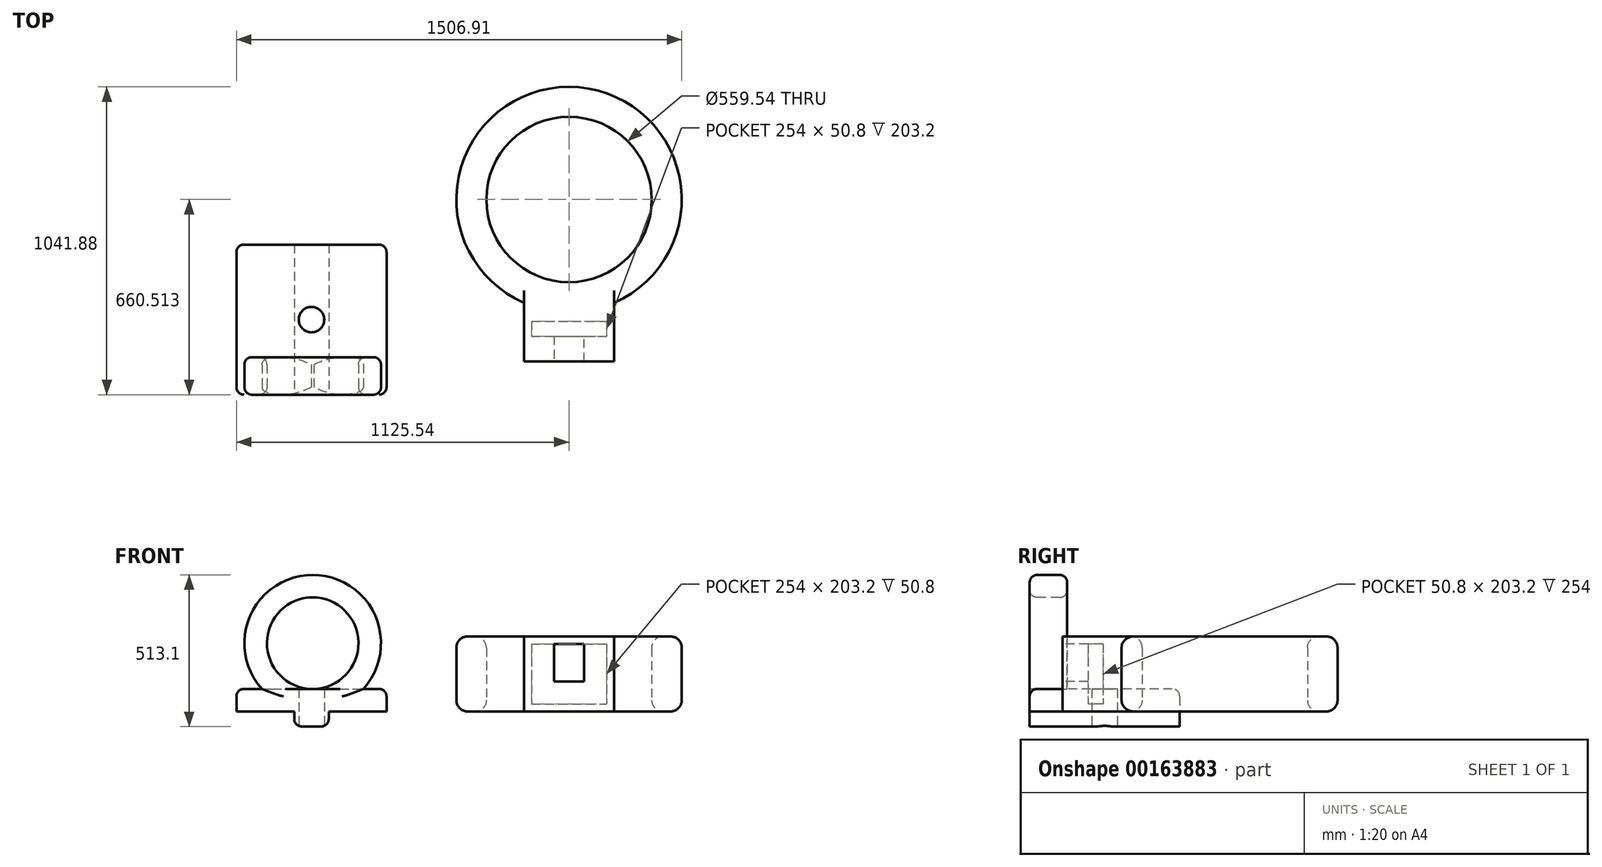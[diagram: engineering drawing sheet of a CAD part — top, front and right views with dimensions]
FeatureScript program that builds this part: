
annotation { "Feature Type Name" : "Feature", "Feature Type Description" : "" }
export const myFeature = defineFeature(function(context is Context, id is Id, definition is map)
    precondition{}
    {
        {
            var Q0;
            Q0=qCreatedBy(makeId("Top.planeOp"),FACE);
            var sketch = newSketch(context, id + "F0", { "sketchPlane" : qUnion([Q0])});
            skLineSegment(sketch, "E0.bottom", {"start": v(-152.4, 196.86) * mm, "end": v(152.4, 196.86) * mm});
            skLineSegment(sketch, "E0.top", {"start": v(-152.4, -6.34) * mm, "end": v(152.4, -6.34) * mm});
            skLineSegment(sketch, "E0.left", {"start": v(-152.4, 196.86) * mm, "end": v(-152.4, -6.34) * mm});
            skLineSegment(sketch, "E0.right", {"start": v(152.4, 196.86) * mm, "end": v(152.4, -6.34) * mm});
            skCircle(sketch, "E1", {"center": v(0, 542.32) * mm, "radius": 381.37 * mm});
            skCircle(sketch, "E2", {"center": v(0, 542.32) * mm, "radius": 279.77 * mm});
            skSolve(sketch);
        }
        {
            var Q0;
            {var subQ5=sQuery(id+"F0.wireOp",EDGE,"E0.bottom");Q0=makeQuery(id+"F0.imprint","IMPRINT",FACE,{"disambiguationData":[TD([[makeQuery(id+"F0.imprint","IMPRINT",EDGE,{"derivedFrom":subQ5}),1.0]])]});}
            var Q1;
            {var subQ0=sQuery(id+"F0.wireOp",EDGE,"E0.bottom");Q1=makeQuery(id+"F0.imprint","IMPRINT",FACE,{"disambiguationData":[TD([[makeQuery(id+"F0.imprint","IMPRINT",EDGE,{"derivedFrom":subQ0}),-1.0]])]});}
            var Q2;
            {var subQ0=sQuery(id+"F0.wireOp",EDGE,"E0.top");Q2=makeQuery(id+"F0.imprint","IMPRINT",FACE,{"disambiguationData":[TD([[makeQuery(id+"F0.imprint","IMPRINT",EDGE,{"derivedFrom":subQ0}),1.0]])]});}
            extrude(context, id + "F1", {"entities" : qUnion([Q0, Q1, Q2]), "depth" : 25.4 * mm});
        }
        {
            var Q0;
            Q0=makeQuery(id+"F1.opExtrude","CAP_FACE",FACE,{"disambiguationData":[OSD([sQuery(id+"F0.wireOp",EDGE,"E0.top"),sQuery(id+"F0.wireOp",EDGE,"E0.left"),sQuery(id+"F0.wireOp",EDGE,"E0.right"),sQuery(id+"F0.wireOp",EDGE,"E1"),sQuery(id+"F0.wireOp",EDGE,"E2")])],"isStart":false});
            var sketch = newSketch(context, id + "F2", { "sketchPlane" : qUnion([Q0])});
            skLineSegment(sketch, "E3.bottom", {"start": v(-127, 130.37) * mm, "end": v(127, 130.37) * mm});
            skLineSegment(sketch, "E3.top", {"start": v(-127, 79.57) * mm, "end": v(127, 79.57) * mm});
            skLineSegment(sketch, "E3.left", {"start": v(-127, 130.37) * mm, "end": v(-127, 79.57) * mm});
            skLineSegment(sketch, "E3.right", {"start": v(127, 130.37) * mm, "end": v(127, 79.57) * mm});
            skSolve(sketch);
        }
        {
            var Q0;
            Q0=makeQuery(id+"F2.imprint","IMPRINT",FACE,{"disambiguationData":[TD([[makeQuery(id+"F2.imprint","IMPRINT",EDGE,{"derivedFrom":sQuery(id+"F2.wireOp",EDGE,"E3.bottom")}),1.0]])]});
            extrude(context, id + "F3", {"entities" : qUnion([Q0]), "operationType" : NewBodyOperationType.ADD, "depth" : 76.2 * mm});
        }
        {
            var Q0;
            Q0=makeQuery(id+"F3.opExtrude","CAP_FACE",FACE,{"disambiguationData":[OSD([sQuery(id+"F0.wireOp",EDGE,"E0.top"),sQuery(id+"F0.wireOp",EDGE,"E0.left"),sQuery(id+"F0.wireOp",EDGE,"E0.right"),sQuery(id+"F0.wireOp",EDGE,"E1"),sQuery(id+"F0.wireOp",EDGE,"E2"),sQuery(id+"F2.wireOp",EDGE,"E3.bottom"),sQuery(id+"F2.wireOp",EDGE,"E3.top"),sQuery(id+"F2.wireOp",EDGE,"E3.left"),sQuery(id+"F2.wireOp",EDGE,"E3.right")])],"isStart":false});
            var sketch = newSketch(context, id + "F4", { "sketchPlane" : qUnion([Q0])});
            skLineSegment(sketch, "E4", {"start": v(-50.8, 79.57) * mm, "end": v(-50.8, -6.34) * mm});
            skLineSegment(sketch, "E5", {"start": v(50.8, -6.34) * mm, "end": v(50.8, 79.57) * mm});
            skSolve(sketch);
        }
        {
            var Q0;
            {var subQ2=sQuery(id+"F4.wireOp",EDGE,"E4");Q0=makeQuery(id+"F4.imprint","IMPRINT",FACE,{"disambiguationData":[TD([[makeQuery(id+"F4.imprint","IMPRINT",EDGE,{"derivedFrom":subQ2}),-1.0]])]});}
            extrude(context, id + "F5", {"entities" : qUnion([Q0]), "operationType" : NewBodyOperationType.ADD, "depth" : 127 * mm});
        }
        {
            var Q0;
            Q0=makeQuery(id+"F5.opExtrude","CAP_FACE",FACE,{"disambiguationData":[OSD([sQuery(id+"F0.wireOp",EDGE,"E0.top"),sQuery(id+"F0.wireOp",EDGE,"E0.left"),sQuery(id+"F0.wireOp",EDGE,"E0.right"),sQuery(id+"F0.wireOp",EDGE,"E1"),sQuery(id+"F0.wireOp",EDGE,"E2"),sQuery(id+"F2.wireOp",EDGE,"E3.bottom"),sQuery(id+"F2.wireOp",EDGE,"E3.top"),sQuery(id+"F2.wireOp",EDGE,"E3.left"),sQuery(id+"F2.wireOp",EDGE,"E3.right"),sQuery(id+"F4.wireOp",EDGE,"E4"),sQuery(id+"F4.wireOp",EDGE,"E5")])],"isStart":false});
            var sketch = newSketch(context, id + "F6", { "sketchPlane" : qUnion([Q0])});
            skLineSegment(sketch, "E6.bottom", {"start": v(-134.74, 146.13) * mm, "end": v(132.82, 146.13) * mm});
            skLineSegment(sketch, "E6.top", {"start": v(-134.74, -6.34) * mm, "end": v(132.82, -6.34) * mm});
            skLineSegment(sketch, "E6.left", {"start": v(-134.74, 146.13) * mm, "end": v(-134.74, -6.34) * mm});
            skLineSegment(sketch, "E6.right", {"start": v(132.82, 146.13) * mm, "end": v(132.82, -6.34) * mm});
            skSolve(sketch);
        }
        {
            var Q0;
            Q0=makeQuery(id+"F6.imprint","IMPRINT",FACE,{"disambiguationData":[TD([[makeQuery(id+"F6.imprint","IMPRINT",EDGE,{"derivedFrom":sQuery(id+"F6.wireOp",EDGE,"E6.bottom")}),1.0]])]});
            var Q1;
            Q1=makeQuery(id+"F6.imprint","IMPRINT",FACE,{"disambiguationData":[TD([[makeQuery(id+"F6.imprint","IMPRINT",EDGE,{"derivedFrom":sQuery(id+"F6.wireOp",EDGE,"E6.bottom")}),-1.0]])]});
            var Q2;
            {var subQ2=sQuery(id+"F4.wireOp",EDGE,"E4");var subQ3=makeQuery(id+"F5.opExtrude","CAP_EDGE",EDGE,{"disambiguationData":[OSD([subQ2])],"isStart":false});Q2=makeQuery(id+"F6.imprint","IMPRINT",FACE,{"disambiguationData":[TD([[makeQuery(id+"F6.imprint","IMPRINT",EDGE,{"derivedFrom":subQ3}),1.0]])]});}
            extrude(context, id + "F7", {"entities" : qUnion([Q0, Q1, Q2]), "operationType" : NewBodyOperationType.ADD, "depth" : 25.4 * mm});
        }
        {
            var Q0;
            Q0=makeQuery(id+"F7.opExtrude","CAP_EDGE",EDGE,{"disambiguationData":[OSD([sQuery(id+"F0.wireOp",EDGE,"E1")])],"isStart":false});
            var Q1;
            Q1=makeQuery(id+"F1.opExtrude","CAP_EDGE",EDGE,{"disambiguationData":[OSD([sQuery(id+"F0.wireOp",EDGE,"E1")])],"isStart":true});
            var Q2;
            Q2=makeQuery(id+"F7.opExtrude","CAP_EDGE",EDGE,{"disambiguationData":[OSD([sQuery(id+"F0.wireOp",EDGE,"E2")])],"isStart":false});
            var Q3;
            Q3=makeQuery(id+"F1.opExtrude","CAP_EDGE",EDGE,{"disambiguationData":[OSD([sQuery(id+"F0.wireOp",EDGE,"E2")])],"isStart":true});
            fillet(context, id + "F8", {"entities" : qUnion([Q0, Q1, Q2, Q3]), "radius" : 38.1 * mm, "tangentPropagation" : true, "allowEdgeOverflow" : false});
        }
        {
            var Q0;
            Q0=qCreatedBy(makeId("Top.planeOp"),FACE);
            var sketch = newSketch(context, id + "F9", { "sketchPlane" : qUnion([Q0])});
            skLineSegment(sketch, "E7.bottom", {"start": v(-1125.54, 389.8) * mm, "end": v(-617.54, 389.8) * mm});
            skLineSegment(sketch, "E7.top", {"start": v(-1125.54, -118.2) * mm, "end": v(-617.54, -118.2) * mm});
            skLineSegment(sketch, "E7.left", {"start": v(-1125.54, 389.8) * mm, "end": v(-1125.54, -118.2) * mm});
            skLineSegment(sketch, "E7.right", {"start": v(-617.54, 389.8) * mm, "end": v(-617.54, -118.2) * mm});
            skCircle(sketch, "E8", {"center": v(-871.54, 135.8) * mm, "radius": 43.18 * mm});
            skPoint(sketch, "E8.centerSnap0", {"position": v(-871.54, 389.8) * mm});
            skPoint(sketch, "E8.centerSnap1", {"position": v(-1125.54, 135.8) * mm});
            skLineSegment(sketch, "E9.bottom", {"start": v(-929.96, 389.8) * mm, "end": v(-813.12, 389.8) * mm});
            skLineSegment(sketch, "E9.top", {"start": v(-929.96, -118.2) * mm, "end": v(-813.12, -118.2) * mm});
            skLineSegment(sketch, "E9.left", {"start": v(-929.96, 389.8) * mm, "end": v(-929.96, -118.2) * mm});
            skLineSegment(sketch, "E9.right", {"start": v(-813.12, 389.8) * mm, "end": v(-813.12, -118.2) * mm});
            skSolve(sketch);
        }
        {
            var Q0;
            {var subQ0=sQuery(id+"F9.wireOp",EDGE,"E7.left");Q0=makeQuery(id+"F9.imprint","IMPRINT",FACE,{"disambiguationData":[TD([[makeQuery(id+"F9.imprint","IMPRINT",EDGE,{"derivedFrom":subQ0}),1.0]])]});}
            var Q1;
            Q1=makeQuery(id+"F9.imprint","IMPRINT",FACE,{"disambiguationData":[TD([[makeQuery(id+"F9.imprint","IMPRINT",EDGE,{"derivedFrom":sQuery(id+"F9.wireOp",EDGE,"E8")}),-1.0]])]});
            var Q2;
            {var subQ2=sQuery(id+"F9.wireOp",EDGE,"E7.right");Q2=makeQuery(id+"F9.imprint","IMPRINT",FACE,{"disambiguationData":[TD([[makeQuery(id+"F9.imprint","IMPRINT",EDGE,{"derivedFrom":subQ2}),-1.0]])]});}
            extrude(context, id + "F10", {"entities" : qUnion([Q0, Q1, Q2]), "depth" : 76.2 * mm});
        }
        {
            var Q0;
            Q0=makeQuery(id+"F9.imprint","IMPRINT",FACE,{"disambiguationData":[TD([[makeQuery(id+"F9.imprint","IMPRINT",EDGE,{"derivedFrom":sQuery(id+"F9.wireOp",EDGE,"E8")}),-1.0]])]});
            extrude(context, id + "F11", {"entities" : qUnion([Q0]), "operationType" : NewBodyOperationType.ADD, "oppositeDirection" : true, "depth" : 50.8 * mm});
        }
        {
            var Q0;
            Q0=makeQuery(id+"F11.opExtrude","CAP_EDGE",EDGE,{"disambiguationData":[OSD([sQuery(id+"F9.wireOp",EDGE,"E9.left")])],"isStart":false});
            var Q1;
            Q1=makeQuery(id+"F11.opExtrude","CAP_EDGE",EDGE,{"disambiguationData":[OSD([sQuery(id+"F9.wireOp",EDGE,"E9.right")])],"isStart":false});
            var Q2;
            Q2=makeQuery(id+"F10.opExtrude","SWEPT_EDGE",EDGE,{"disambiguationData":[OSD([sQuery(id+"F9.wireOp",EDGE,"E7.bottom"),sQuery(id+"F9.wireOp",EDGE,"E7.left")])]});
            var Q3;
            Q3=makeQuery(id+"F10.opExtrude","SWEPT_EDGE",EDGE,{"disambiguationData":[OSD([sQuery(id+"F9.wireOp",EDGE,"E7.bottom"),sQuery(id+"F9.wireOp",EDGE,"E7.right")])]});
            var Q4;
            Q4=makeQuery(id+"F10.opExtrude","SWEPT_EDGE",EDGE,{"disambiguationData":[OSD([sQuery(id+"F9.wireOp",EDGE,"E7.top"),sQuery(id+"F9.wireOp",EDGE,"E7.left")])]});
            var Q5;
            Q5=makeQuery(id+"F10.opExtrude","SWEPT_EDGE",EDGE,{"disambiguationData":[OSD([sQuery(id+"F9.wireOp",EDGE,"E7.top"),sQuery(id+"F9.wireOp",EDGE,"E7.right")])]});
            fillet(context, id + "F12", {"entities" : qUnion([Q0, Q1, Q2, Q3, Q4, Q5]), "radius" : 25.4 * mm, "tangentPropagation" : true, "allowEdgeOverflow" : false});
        }
        {
            var Q0;
            {var subQ0=sQuery(id+"F9.wireOp",EDGE,"E7.top");Q0=makeQuery(id+"F11.boolean.opBoolean","MERGE",FACE,{"derivedFrom":[makeQuery(id+"F10.opExtrude","SWEPT_FACE",FACE,{"disambiguationData":[OSD([subQ0])]}),makeQuery(id+"F11.opExtrude","SWEPT_FACE",FACE,{"disambiguationData":[OSD([subQ0])]})]});}
            var sketch = newSketch(context, id + "F13", { "sketchPlane" : qUnion([Q0])});
            skCircle(sketch, "E10", {"center": v(-867.45, 231.12) * mm, "radius": 231.18 * mm});
            skPoint(sketch, "E10.first.point", {"position": v(-872.57, 0) * mm});
            skPoint(sketch, "E10.second.point", {"position": v(-863.35, 462.26) * mm});
            skPoint(sketch, "E10.third.point", {"position": v(-871.54, 462.26) * mm});
            skPoint(sketch, "E10.third.point.positionSnap0", {"position": v(-871.54, 76.2) * mm});
            skCircle(sketch, "E11", {"center": v(-867.45, 231.12) * mm, "radius": 154.98 * mm});
            skSolve(sketch);
        }
        {
            var Q0;
            {var subQ0=sQuery(id+"F13.wireOp",EDGE,"E10");var subQ1=makeQuery(id+"F10.opExtrude","CAP_EDGE",EDGE,{"disambiguationData":[OSD([sQuery(id+"F9.wireOp",EDGE,"E7.top")])],"isStart":false});var subQ2=makeQuery(id+"F13.imprint","INTERSECT",VERTEX,{"disambiguationData":[OD(0.0)],"derivedFrom":[subQ1,subQ0]});Q0=makeQuery(id+"F13.imprint","IMPRINT",FACE,{"disambiguationData":[TD([[makeQuery(id+"F13.imprint","IMPRINT",EDGE,{"disambiguationData":[TD([[subQ2,1.0]])],"derivedFrom":subQ0}),1.0]])]});}
            extrude(context, id + "F14", {"entities" : qUnion([Q0]), "operationType" : NewBodyOperationType.ADD, "oppositeDirection" : true, "depth" : 127 * mm});
        }
        {
            var Q0;
            Q0=makeQuery(id+"F14.opExtrude","CAP_EDGE",EDGE,{"disambiguationData":[OSD([sQuery(id+"F13.wireOp",EDGE,"E11")])],"isStart":false});
            var Q1;
            Q1=makeQuery(id+"F14.opExtrude","CAP_EDGE",EDGE,{"disambiguationData":[OSD([sQuery(id+"F13.wireOp",EDGE,"E10")])],"isStart":false});
            var Q2;
            Q2=makeQuery(id+"F14.opExtrude","CAP_EDGE",EDGE,{"disambiguationData":[OSD([sQuery(id+"F13.wireOp",EDGE,"E10")])],"isStart":true});
            var Q3;
            Q3=makeQuery(id+"F14.opExtrude","CAP_EDGE",EDGE,{"disambiguationData":[OSD([sQuery(id+"F13.wireOp",EDGE,"E11")])],"isStart":true});
            var Q4;
            Q4=makeQuery(id+"F10.opExtrude","CAP_EDGE",EDGE,{"disambiguationData":[OSD([sQuery(id+"F9.wireOp",EDGE,"E7.left")])],"isStart":false});
            fillet(context, id + "F15", {"entities" : qUnion([Q0, Q1, Q2, Q3, Q4]), "radius" : 25.4 * mm, "tangentPropagation" : true, "allowEdgeOverflow" : false});
        }
    });
